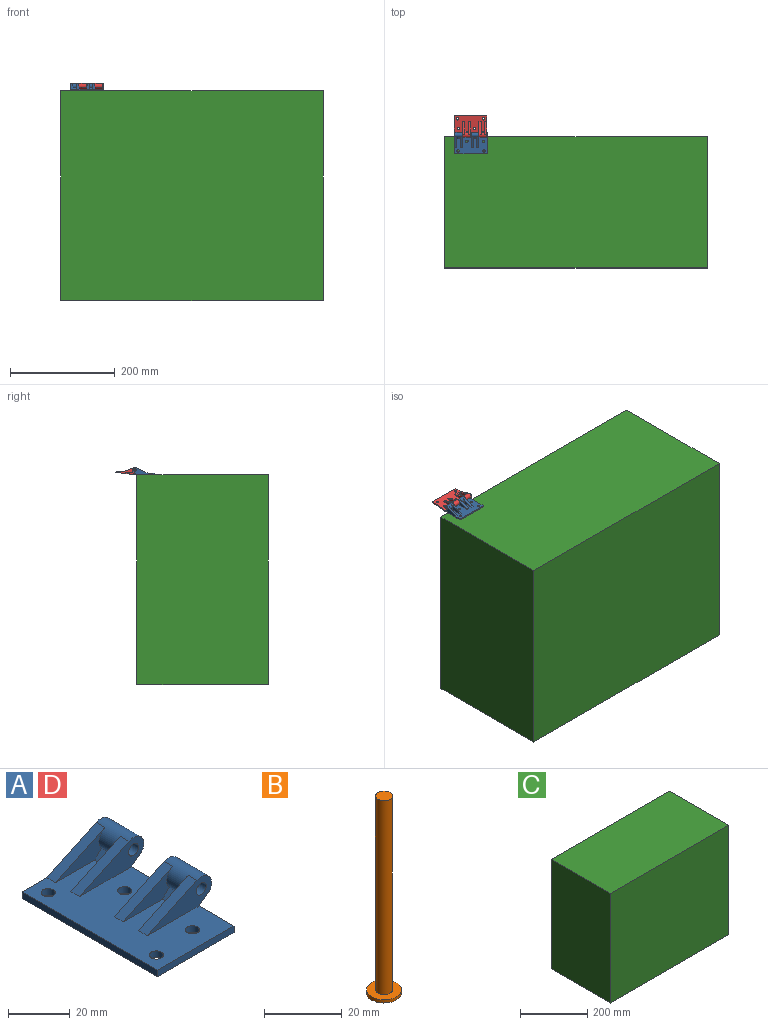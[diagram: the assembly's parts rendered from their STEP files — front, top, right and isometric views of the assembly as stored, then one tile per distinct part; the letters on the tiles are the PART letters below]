
ASSEMBLY  parts=4 mates=3
PART A: 29 faces, bbox 40.8x62x13.7 mm
  f0: plane 7x3.17mm, normal (-0.71,0,0.71), area 31.4mm2, adj f1,f3,f26,f28
  f1: cylinder r=4.77mm len=15mm, axis (0,1,0), area 240.4mm2, adj f0,f5,f9,f11,f25,f26,f27,f28
  f2: plane 7x3.17mm, normal (-0.71,0,0.71), area 31.4mm2, adj f3,f4,f22,f24
  f3: plane 62x35mm, normal (0,0,1), area 1645.1mm2, adj f0,f2,f5,f6,f8,f11,f12,f15
  f4: cylinder r=4.77mm len=15mm, axis (0,-1,0), area 240.4mm2, adj f2,f13,f15,f16,f21,f22,f23,f24
  f5: plane 29.44x11.05mm, normal (0,-1,0), area 160.5mm2, adj f1,f3,f9,f10,f27
  f6: plane 62x2.6mm, normal (-1,0,0), area 161.2mm2, adj f3,f7,f12,f15
  f7: plane 62x35mm, normal (0,0,-1), area 2105mm2, adj f6,f8,f12,f15,f17,f18,f19,f20
  f8: plane 62x2.6mm, normal (1,0,0), area 161.2mm2, adj f3,f7,f9,f12,f13,f15
  f9: plane 15x5.22mm, normal (0.61,0,-0.79), area 98.9mm2, adj f1,f5,f8,f11
  f10: cylinder r=2.27mm len=15mm, axis (0,1,0), area 214.4mm2, adj f5,f11
  f11: plane 29.44x11.05mm, normal (0,1,0), area 160.5mm2, adj f1,f3,f9,f10,f25
  f12: plane 35x2.6mm, normal (0,-1,0), area 91mm2, adj f3,f6,f7,f8
  f13: plane 15x5.22mm, normal (0.61,0,-0.79), area 98.9mm2, adj f4,f8,f15,f16
  f14: cylinder r=2.27mm len=15mm, axis (0,-1,0), area 214.4mm2, adj f15,f16
  f15: plane 40.78x13.65mm, normal (0,1,0), area 251.5mm2, adj f3,f4,f6,f7,f8,f13,f14,f21
  f16: plane 29.44x11.05mm, normal (0,-1,0), area 160.5mm2, adj f3,f4,f13,f14,f23
  f17: cylinder r=2.27mm len=4.55mm, axis (0,0,1), area 37.2mm2, adj f3,f7
  f18: cylinder r=2.27mm len=4.55mm, axis (0,0,1), area 37.2mm2, adj f3,f7
  f19: cylinder r=2.27mm len=4.55mm, axis (0,0,1), area 37.2mm2, adj f3,f7
  f20: cylinder r=2.27mm len=4.55mm, axis (0,0,1), area 37.2mm2, adj f3,f7
  f21: plane 22.64x10.6mm, normal (-0.42,0,0.91), area 100mm2, adj f3,f4,f15,f22
  f22: plane 22.64x10.6mm, normal (0,-1,0), area 93.9mm2, adj f2,f3,f4,f21
  f23: plane 22.64x10.6mm, normal (-0.42,0,0.91), area 100mm2, adj f3,f4,f16,f24
  f24: plane 22.64x10.6mm, normal (0,1,0), area 93.9mm2, adj f2,f3,f4,f23
  f25: plane 22.64x10.6mm, normal (-0.42,0,0.91), area 100mm2, adj f1,f3,f11,f26
  f26: plane 22.64x10.6mm, normal (0,-1,0), area 93.9mm2, adj f0,f1,f3,f25
  f27: plane 22.64x10.6mm, normal (-0.42,0,0.91), area 100mm2, adj f1,f3,f5,f28
  f28: plane 22.64x10.6mm, normal (0,1,0), area 93.9mm2, adj f0,f1,f3,f27
PART B: 5 faces, bbox 9x9x62 mm
  f0: cylinder r=2.19mm len=61mm, axis (0,0,-1), area 837.5mm2, adj f1,f4
  f1: plane 4.37x4.37mm, normal (0,0,1), area 15mm2, adj f0
  f2: cylinder r=4.5mm len=9mm, axis (0,0,1), area 28.3mm2, adj f3,f4
  f3: plane 9x9mm, normal (0,0,-1), area 63.6mm2, adj f2
  f4: plane 9x9mm, normal (0,0,1), area 48.6mm2, adj f0,f2
PART C: 6 faces, bbox 500x250x400 mm
  f0: plane 400x250mm, normal (1,0,0), area 100000mm2, adj f1,f3,f4,f5
  f1: plane 500x400mm, normal (0,1,0), area 200000mm2, adj f0,f2,f4,f5
  f2: plane 400x250mm, normal (-1,0,0), area 100000mm2, adj f1,f3,f4,f5
  f3: plane 500x400mm, normal (0,-1,0), area 200000mm2, adj f0,f2,f4,f5
  f4: plane 500x250mm, normal (0,0,1), area 125000mm2, adj f0,f1,f2,f3
  f5: plane 500x250mm, normal (0,0,-1), area 125000mm2, adj f0,f1,f2,f3
PART D: same geometry as A
PLACE A rot(axis=(0,0,1),90deg) t=(-199.88,127.42,2.6)mm
PLACE B rot(axis=(0.58,-0.58,-0.58),120deg) t=(-169.88,128.42,8.88)mm
PLACE C t=(0,0,-400)mm
PLACE D rot(axis=(0.06,0.06,-1),90.2deg) t=(-200.88,130.16,2.76)mm
MATE revolute D.f1 <-> A.f1  axis (-1,0,0) through (-215.88,128.42,8.88)mm
MATE fastened A.f7 <-> C.f4  axis (0,0,-1) through (-200,110,0)mm
MATE fastened B.f0 <-> A.f1  axis (-1,0,0) through (-230.88,128.42,8.88)mm
